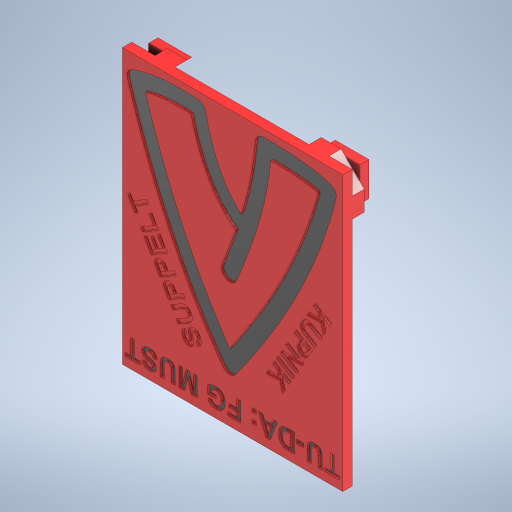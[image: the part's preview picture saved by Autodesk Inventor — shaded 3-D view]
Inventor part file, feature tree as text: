
AUTODESK INVENTOR PART (.ipt)
format: ipt  version: 2023.3 (Build 273359000, 359)  size: 1,052,160 bytes
history: native  units: in
note: dims shown in document units (in); Inventor stores cm internally (conversion verified against a paired STEP export)
features: extrude x7, sketch x7, reference x4, projected_geometry x3, other x3
ambient origin geometry x8: Origin, YZ Plane, XZ Plane, XY Plane, X Axis, Y Axis, Z Axis, Center Point
bodies: Solid1 (feature_tree)
feature tree (24):
  extrude  "Extrusion1"  Depth=0.0787in TaperAngle=0.0deg
  extrude  "Extrusion2"  Depth=0.0236in
  extrude  "Extrusion3"  Depth=0.1181in
  extrude  "Extrusion4"  Depth=0.0787in TaperAngle=0.0deg
  extrude  "Extrusion5"  Depth=0.1575in
  extrude  "Extrusion6"  Depth=0.1575in
  extrude  "Extrusion7"  Depth=0.0157in TaperAngle=0.0deg
  sketch  "Sketch1"  dims[d0=0.0079in d1=0.0787in d2=0.0in]
  reference  "Reference1"
  sketch  "Sketch2"  dims[d3=0.0236in d4=0.0236in]
  reference  "Reference2"
  reference  "Reference3"
  reference  "Reference4"
  sketch  "Sketch3"  dims[d5=0.1181in d6=0.1181in]
  projected_geometry  "Projected Loop1"
  projected_geometry  "Projected Loop2"
  sketch  "Sketch6"  dims[d7=0.1024in d8=0.0in d9=0.0787in d10=0.0in]
  sketch  "Sketch7"  dims[d11=0.0394in d12=0.1575in]
  sketch  "Sketch8"  dims[d13=0.315in d14=0.1575in]
  projected_geometry  "Projected Loop3"
  sketch  "Skizze9"  dims[d15=0.1575in d16=0.0in d17=0.0157in d18=0.0in d19=0.0157in d20=0.0in d21=1.0148in d22=1.0148in d23=0.1601in d24=0.1601in d25=30.0deg d26=30.0deg d27=0.9055in d28=0.4331in d29=0.4331in d30=0.0157in d31=0.0in]
  other  "<userpath>\Documents\Github\Acoustifly\CAD\1_Col_Print\Assembly.iam"
  other  "Assembly.iam"
  other  "Base:1"
